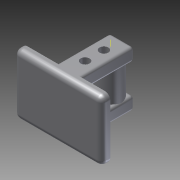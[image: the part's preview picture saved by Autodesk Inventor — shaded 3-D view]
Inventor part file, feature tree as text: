
AUTODESK INVENTOR PART (.ipt)
format: ipt  version: 2012 (Build 160160000, 160)  size: 376,320 bytes
history: native  units: in
note: dims shown in document units (in); Inventor stores cm internally (conversion verified against a paired STEP export)
features: fillet x10, extrude x6, sketch x6, other x4, projected_geometry x3
ambient origin geometry x8: Origin, YZ Plane, XZ Plane, XY Plane, X Axis, Y Axis, Z Axis, Center Point
bodies: Solid1 (feature_tree)
feature tree (29):
  other  "TopAndIntermediaryAxle"
  other  "GearBoxTop.ipt:1"
  other  "LargeSmallGearAxis.ipt:1"
  extrude  "Extrusion1"  Depth=0.3937in TaperAngle=0.0deg
  extrude  "Extrusion2"  Depth=0.0787in
  fillet  "Fillet1"  Radius=0.0787in
  fillet  "Fillet2"  Radius=0.0787in
  fillet  "Fillet3"  Radius=0.0787in
  fillet  "Fillet4"  Radius=0.0787in
  fillet  "Fillet5"  Radius=0.0394in
  fillet  "Fillet6"  Radius=0.0394in
  fillet  "Fillet7"  Radius=0.0394in
  fillet  "Fillet8"  Radius=0.0394in
  fillet  "Fillet9"  Radius=0.0394in
  fillet  "Fillet10"  Radius=0.269in
  extrude  "Extrusion4"  Depth=0.1181in TaperAngle=0.0deg
  extrude  "Extrusion5"  Depth=0.2657in
  extrude  "Extrusion3"  Depth=0.1329in
  extrude  "Extrusion6"  Depth=0.126in
  other  "Work Axis1"
  sketch  "Sketch2"  dims[d0=0.3937in d1=0.3937in d2=0.0in]
  projected_geometry  "Projected Loop1"
  sketch  "Sketch3"  dims[d3=0.3937in d4=0.0in d5=0.0787in d6=0.0787in d7=0.0787in d8=0.0787in d9=0.0787in d10=0.0394in d11=0.0394in d12=0.0394in d13=0.0394in d14=0.0394in d15=0.269in]
  projected_geometry  "Projected Loop2"
  sketch  "Sketch4"  dims[d18=0.7964in d19=0.1181in d20=0.0in]
  projected_geometry  "Projected Loop3"
  sketch  "Sketch5"  dims[d21=0.1181in d22=0.0in d23=0.2657in]
  sketch  "Sketch6"  dims[d24=0.1329in d25=0.1329in]
  sketch  "Sketch7"  dims[d26=0.126in d27=0.126in d28=0.1181in d29=0.0in d30=0.269in d31=0.1181in d32=0.0in]
